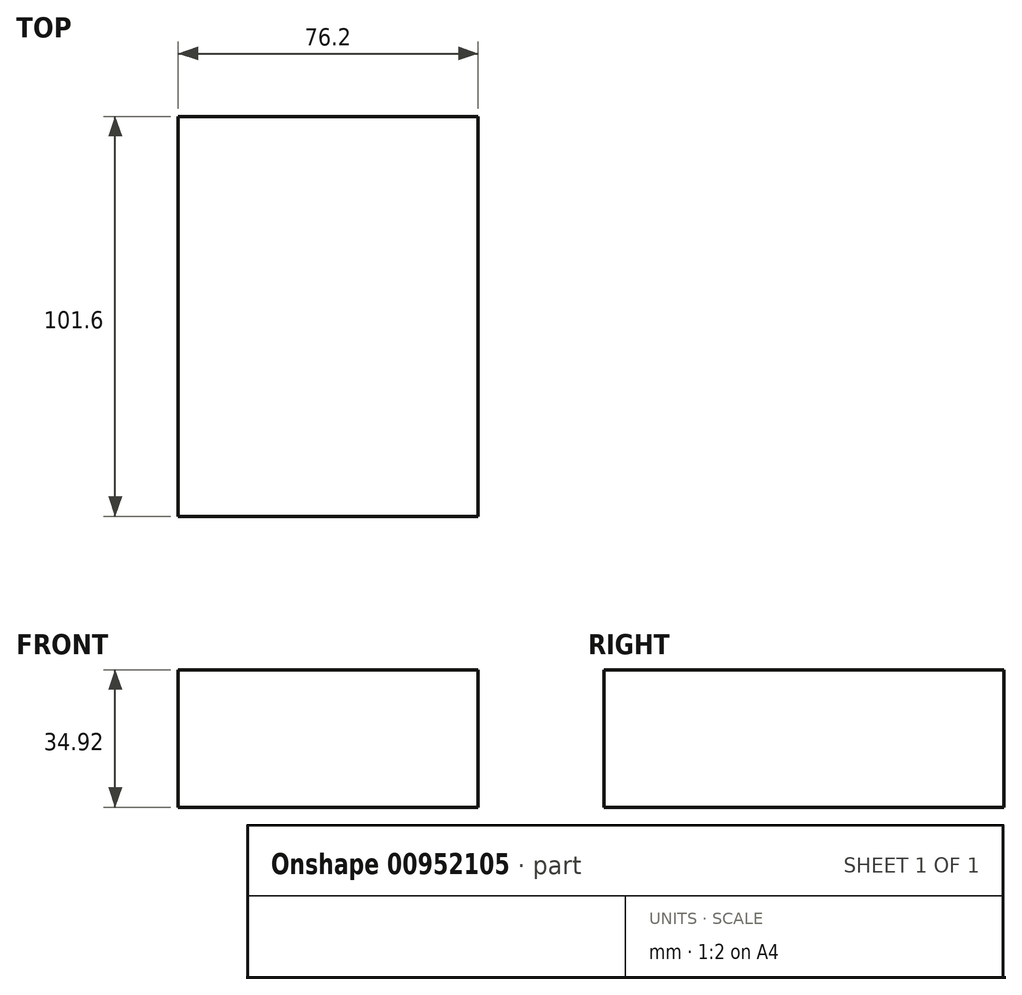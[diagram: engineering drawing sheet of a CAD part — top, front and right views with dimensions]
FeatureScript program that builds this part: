
annotation { "Feature Type Name" : "Feature", "Feature Type Description" : "" }
export const myFeature = defineFeature(function(context is Context, id is Id, definition is map)
    precondition{}
    {
        {
            var Q0;
            Q0=qCreatedBy(makeId("Top.planeOp"),FACE);
            var sketch = newSketch(context, id + "F0", { "sketchPlane" : qUnion([Q0])});
            skLineSegment(sketch, "E0.bottom", {"start": v(-38.1, 50.8) * mm, "end": v(38.1, 50.8) * mm});
            skLineSegment(sketch, "E0.top", {"start": v(-38.1, -50.8) * mm, "end": v(38.1, -50.8) * mm});
            skLineSegment(sketch, "E0.left", {"start": v(-38.1, 50.8) * mm, "end": v(-38.1, -50.8) * mm});
            skLineSegment(sketch, "E0.right", {"start": v(38.1, 50.8) * mm, "end": v(38.1, -50.8) * mm});
            skLineSegment(sketch, "E1", {"start": v(-38.1, 50.8) * mm, "end": v(38.1, -50.8) * mm});
            skSolve(sketch);
        }
        {
            var Q0;
            Q0 = qSketchRegion(id + "F0", true);
            extrude(context, id + "F1", {"entities" : qUnion([Q0]), "depth" : 34.92 * mm, "offsetDistance" : 25.4 * mm});
        }
    });
